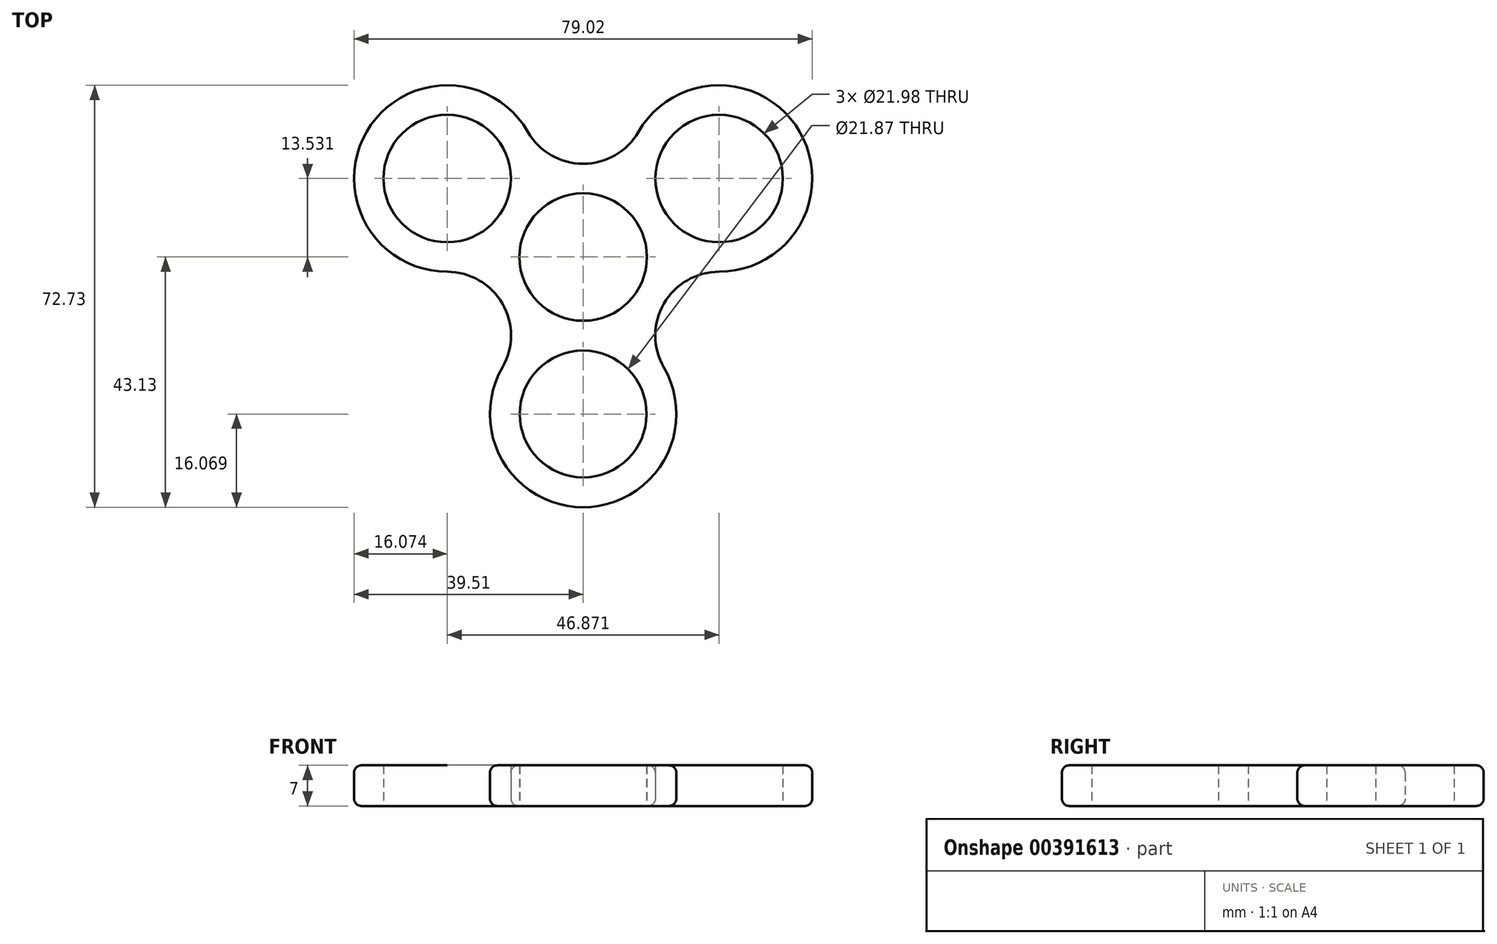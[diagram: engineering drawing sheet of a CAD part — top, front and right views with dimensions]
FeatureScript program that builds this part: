
annotation { "Feature Type Name" : "Feature", "Feature Type Description" : "" }
export const myFeature = defineFeature(function(context is Context, id is Id, definition is map)
    precondition{}
    {
        {
            var Q0;
            Q0=qCreatedBy(makeId("Top.planeOp"),FACE);
            var sketch = newSketch(context, id + "F0", { "sketchPlane" : qUnion([Q0])});
            skArc(sketch, "E0", {"start": v(0, 11) * mm, "mid": v(-5.5, -9.52) * mm, "end": v(9.52, 5.5) * mm, "construction": true});
            skLineSegment(sketch, "E1", {"start": v(0, 0) * mm, "end": v(92.12, 53.18) * mm, "construction": true});
            skLineSegment(sketch, "E2", {"start": v(0, 0) * mm, "end": v(-9.52, 5.5) * mm, "construction": true});
            skLineSegment(sketch, "E3", {"start": v(0, 0) * mm, "end": v(0, -70.87) * mm, "construction": true});
            skCircle(sketch, "E4", {"center": v(-23.44, 13.53) * mm, "radius": 11 * mm, "construction": true});
            skArc(sketch, "E5", {"start": v(13.92, 8.04) * mm, "mid": v(28.93, 4.01) * mm, "end": v(32.95, 19.03) * mm, "construction": true});
            skCircle(sketch, "E6", {"center": v(0, -27.06) * mm, "radius": 11 * mm, "construction": true});
            skLineSegment(sketch, "E7", {"start": v(0, 0) * mm, "end": v(-69.62, -40.2) * mm, "construction": true});
            skLineSegment(sketch, "E8", {"start": v(0, 0) * mm, "end": v(71.9, -41.52) * mm, "construction": true});
            skLineSegment(sketch, "E9", {"start": v(0, 0) * mm, "end": v(0, 11) * mm, "construction": true});
            skLineSegment(sketch, "E10", {"start": v(-23.44, 13.53) * mm, "end": v(-12.14, 33.1) * mm, "construction": true});
            skLineSegment(sketch, "E11", {"start": v(23.44, 13.53) * mm, "end": v(12.02, 33.3) * mm, "construction": true});
            skLineSegment(sketch, "E12", {"start": v(-37.35, 21.57) * mm, "end": v(-32.95, 19.03) * mm, "construction": true});
            skLineSegment(sketch, "E13", {"start": v(9.52, 5.5) * mm, "end": v(13.92, 8.04) * mm});
            skLineSegment(sketch, "E14", {"start": v(37.35, 21.57) * mm, "end": v(32.95, 19.03) * mm});
            skArc(sketch, "E15", {"start": v(-9.52, 5.5) * mm, "mid": v(-5.5, 9.52) * mm, "end": v(0, 11) * mm});
            skArc(sketch, "E16", {"start": v(-9.52, 21.57) * mm, "mid": v(-5.5, 17.54) * mm, "end": v(0, 16.07) * mm});
            skArc(sketch, "E17", {"start": v(-32.95, 19.03) * mm, "mid": v(-17.94, 23.05) * mm, "end": v(-13.92, 8.04) * mm});
            skLineSegment(sketch, "E18.trimOffspring", {"start": v(-37.35, 21.57) * mm, "end": v(-92.12, 53.18) * mm, "construction": true});
            skLineSegment(sketch, "E19.trimOffspring", {"start": v(-13.92, 8.04) * mm, "end": v(-32.95, 19.03) * mm, "construction": true});
            skArc(sketch, "E20", {"start": v(-9.52, 21.57) * mm, "mid": v(-23.44, 29.6) * mm, "end": v(-37.35, 21.57) * mm});
            skLineSegment(sketch, "E21", {"start": v(-37.35, 21.57) * mm, "end": v(-32.95, 19.03) * mm});
            skLineSegment(sketch, "E22", {"start": v(-13.92, 8.04) * mm, "end": v(-9.52, 5.5) * mm});
            skPoint(sketch, "E23.start.orphan", {"position": v(23.44, 29.6) * mm});
            skLineSegment(sketch, "E24.trimOffspring", {"start": v(0, 16.07) * mm, "end": v(0, 62.86) * mm, "construction": true});
            skLineSegment(sketch, "E25", {"start": v(0, 16.07) * mm, "end": v(0, 11) * mm});
            skLineSegment(sketch, "E26.MirrorCS", {"start": v(-13.92, -8.04) * mm, "end": v(-9.52, -5.5) * mm});
            skArc(sketch, "E27.MirrorCS", {"start": v(-23.44, -2.54) * mm, "mid": v(-17.94, -4.01) * mm, "end": v(-13.92, -8.04) * mm});
            skArc(sketch, "E28.MirrorCS", {"start": v(-23.44, -2.54) * mm, "mid": v(-37.35, 5.5) * mm, "end": v(-37.35, 21.57) * mm});
            skArc(sketch, "E29.MirrorCS", {"start": v(-9.52, 5.5) * mm, "mid": v(-11, 0) * mm, "end": v(-9.52, -5.5) * mm});
            skArc(sketch, "E30.MirrorCS", {"start": v(-32.95, 19.03) * mm, "mid": v(-28.93, 4.01) * mm, "end": v(-13.92, 8.04) * mm});
            skArc(sketch, "E31.MirrorCS", {"start": v(23.44, -2.54) * mm, "mid": v(37.35, 5.5) * mm, "end": v(37.35, 21.57) * mm});
            skLineSegment(sketch, "E32.MirrorCS", {"start": v(13.92, 8.04) * mm, "end": v(9.52, 5.5) * mm});
            skArc(sketch, "E33.MirrorCS", {"start": v(32.95, 19.03) * mm, "mid": v(17.94, 23.05) * mm, "end": v(13.92, 8.04) * mm});
            skArc(sketch, "E34.MirrorCS", {"start": v(32.95, 19.03) * mm, "mid": v(28.93, 4.01) * mm, "end": v(13.92, 8.04) * mm});
            skLineSegment(sketch, "E35.MirrorCS", {"start": v(13.92, -8.04) * mm, "end": v(9.52, -5.5) * mm});
            skArc(sketch, "E36.MirrorCS", {"start": v(23.44, -2.54) * mm, "mid": v(17.94, -4.01) * mm, "end": v(13.92, -8.04) * mm});
            skLineSegment(sketch, "E37.MirrorCS", {"start": v(37.35, 21.57) * mm, "end": v(32.95, 19.03) * mm, "construction": true});
            skArc(sketch, "E38.MirrorCS", {"start": v(9.52, 5.5) * mm, "mid": v(11, 0) * mm, "end": v(9.52, -5.5) * mm});
            skArc(sketch, "E39.MirrorCS", {"start": v(9.52, 21.57) * mm, "mid": v(23.44, 29.6) * mm, "end": v(37.35, 21.57) * mm});
            skLineSegment(sketch, "E40.MirrorCS", {"start": v(23.44, 13.53) * mm, "end": v(12.14, 33.1) * mm, "construction": true});
            skLineSegment(sketch, "E41.MirrorCS", {"start": v(0, 0) * mm, "end": v(9.52, 5.5) * mm, "construction": true});
            skArc(sketch, "E42.MirrorCS", {"start": v(9.52, 5.5) * mm, "mid": v(5.5, 9.52) * mm, "end": v(0, 11) * mm});
            skArc(sketch, "E43.MirrorCS", {"start": v(9.52, 21.57) * mm, "mid": v(5.5, 17.54) * mm, "end": v(0, 16.07) * mm});
            skCircle(sketch, "E44.MirrorC", {"center": v(23.44, 13.53) * mm, "radius": 11 * mm, "construction": true});
            skLineSegment(sketch, "E45.MirrorCS", {"start": v(13.92, 8.04) * mm, "end": v(32.95, 19.03) * mm, "construction": true});
            skArc(sketch, "E46", {"start": v(-9.52, -5.5) * mm, "mid": v(0, -11) * mm, "end": v(9.52, -5.5) * mm});
            skArc(sketch, "E47.MirrorCS", {"start": v(-13.92, -19.03) * mm, "mid": v(-12.45, -13.53) * mm, "end": v(-13.92, -8.04) * mm});
            skArc(sketch, "E48.MirrorCS", {"start": v(-13.92, -19.03) * mm, "mid": v(-13.92, -35.1) * mm, "end": v(0, -43.13) * mm});
            skArc(sketch, "E49.MirrorCS", {"start": v(13.92, -19.03) * mm, "mid": v(12.45, -13.53) * mm, "end": v(13.92, -8.04) * mm});
            skArc(sketch, "E50.MirrorCS", {"start": v(13.92, -19.03) * mm, "mid": v(13.92, -35.1) * mm, "end": v(0, -43.13) * mm});
            skCircle(sketch, "E51", {"center": v(0, -27.06) * mm, "radius": 10.94 * mm});
            skSolve(sketch);
        }
        {
            var Q0;
            Q0=qSketchRegion(id+"F0",true);
            extrude(context, id + "F1", {"entities" : qUnion([Q0]), "depth" : 7 * mm});
        }
        {
            var Q0;
            Q0=makeQuery(id+"F1.opExtrude","CAP_EDGE",EDGE,{"disambiguationData":[OSD([sQuery(id+"F0.wireOp",EDGE,"E36.MirrorCS"),sQuery(id+"F0.wireOp",EDGE,"E49.MirrorCS")])],"isStart":false});
            var Q1;
            Q1=makeQuery(id+"F1.opExtrude","CAP_EDGE",EDGE,{"disambiguationData":[OSD([sQuery(id+"F0.wireOp",EDGE,"E48.MirrorCS"),sQuery(id+"F0.wireOp",EDGE,"E50.MirrorCS")])],"isStart":false});
            var Q2;
            Q2=makeQuery(id+"F1.opExtrude","CAP_EDGE",EDGE,{"disambiguationData":[OSD([sQuery(id+"F0.wireOp",EDGE,"E27.MirrorCS"),sQuery(id+"F0.wireOp",EDGE,"E47.MirrorCS")])],"isStart":false});
            var Q3;
            Q3=makeQuery(id+"F1.opExtrude","CAP_EDGE",EDGE,{"disambiguationData":[OSD([sQuery(id+"F0.wireOp",EDGE,"E20"),sQuery(id+"F0.wireOp",EDGE,"E28.MirrorCS")])],"isStart":false});
            var Q4;
            Q4=makeQuery(id+"F1.opExtrude","CAP_EDGE",EDGE,{"disambiguationData":[OSD([sQuery(id+"F0.wireOp",EDGE,"E16"),sQuery(id+"F0.wireOp",EDGE,"E43.MirrorCS")])],"isStart":false});
            var Q5;
            Q5=makeQuery(id+"F1.opExtrude","CAP_EDGE",EDGE,{"disambiguationData":[OSD([sQuery(id+"F0.wireOp",EDGE,"E31.MirrorCS"),sQuery(id+"F0.wireOp",EDGE,"E39.MirrorCS")])],"isStart":false});
            var Q6;
            Q6=makeQuery(id+"F1.opExtrude","CAP_EDGE",EDGE,{"disambiguationData":[OSD([sQuery(id+"F0.wireOp",EDGE,"E31.MirrorCS"),sQuery(id+"F0.wireOp",EDGE,"E39.MirrorCS")])],"isStart":true});
            var Q7;
            Q7=makeQuery(id+"F1.opExtrude","CAP_EDGE",EDGE,{"disambiguationData":[OSD([sQuery(id+"F0.wireOp",EDGE,"E36.MirrorCS"),sQuery(id+"F0.wireOp",EDGE,"E49.MirrorCS")])],"isStart":true});
            var Q8;
            Q8=makeQuery(id+"F1.opExtrude","CAP_EDGE",EDGE,{"disambiguationData":[OSD([sQuery(id+"F0.wireOp",EDGE,"E48.MirrorCS"),sQuery(id+"F0.wireOp",EDGE,"E50.MirrorCS")])],"isStart":true});
            var Q9;
            Q9=makeQuery(id+"F1.opExtrude","CAP_EDGE",EDGE,{"disambiguationData":[OSD([sQuery(id+"F0.wireOp",EDGE,"E27.MirrorCS"),sQuery(id+"F0.wireOp",EDGE,"E47.MirrorCS")])],"isStart":true});
            var Q10;
            Q10=makeQuery(id+"F1.opExtrude","CAP_EDGE",EDGE,{"disambiguationData":[OSD([sQuery(id+"F0.wireOp",EDGE,"E20"),sQuery(id+"F0.wireOp",EDGE,"E28.MirrorCS")])],"isStart":true});
            var Q11;
            Q11=makeQuery(id+"F1.opExtrude","CAP_EDGE",EDGE,{"disambiguationData":[OSD([sQuery(id+"F0.wireOp",EDGE,"E16"),sQuery(id+"F0.wireOp",EDGE,"E43.MirrorCS")])],"isStart":true});
            fillet(context, id + "F2", {"entities" : qUnion([Q0, Q1, Q2, Q3, Q4, Q5, Q6, Q7, Q8, Q9, Q10, Q11]), "radius" : 1.27 * mm, "tangentPropagation" : true, "allowEdgeOverflow" : false});
        }
    });
